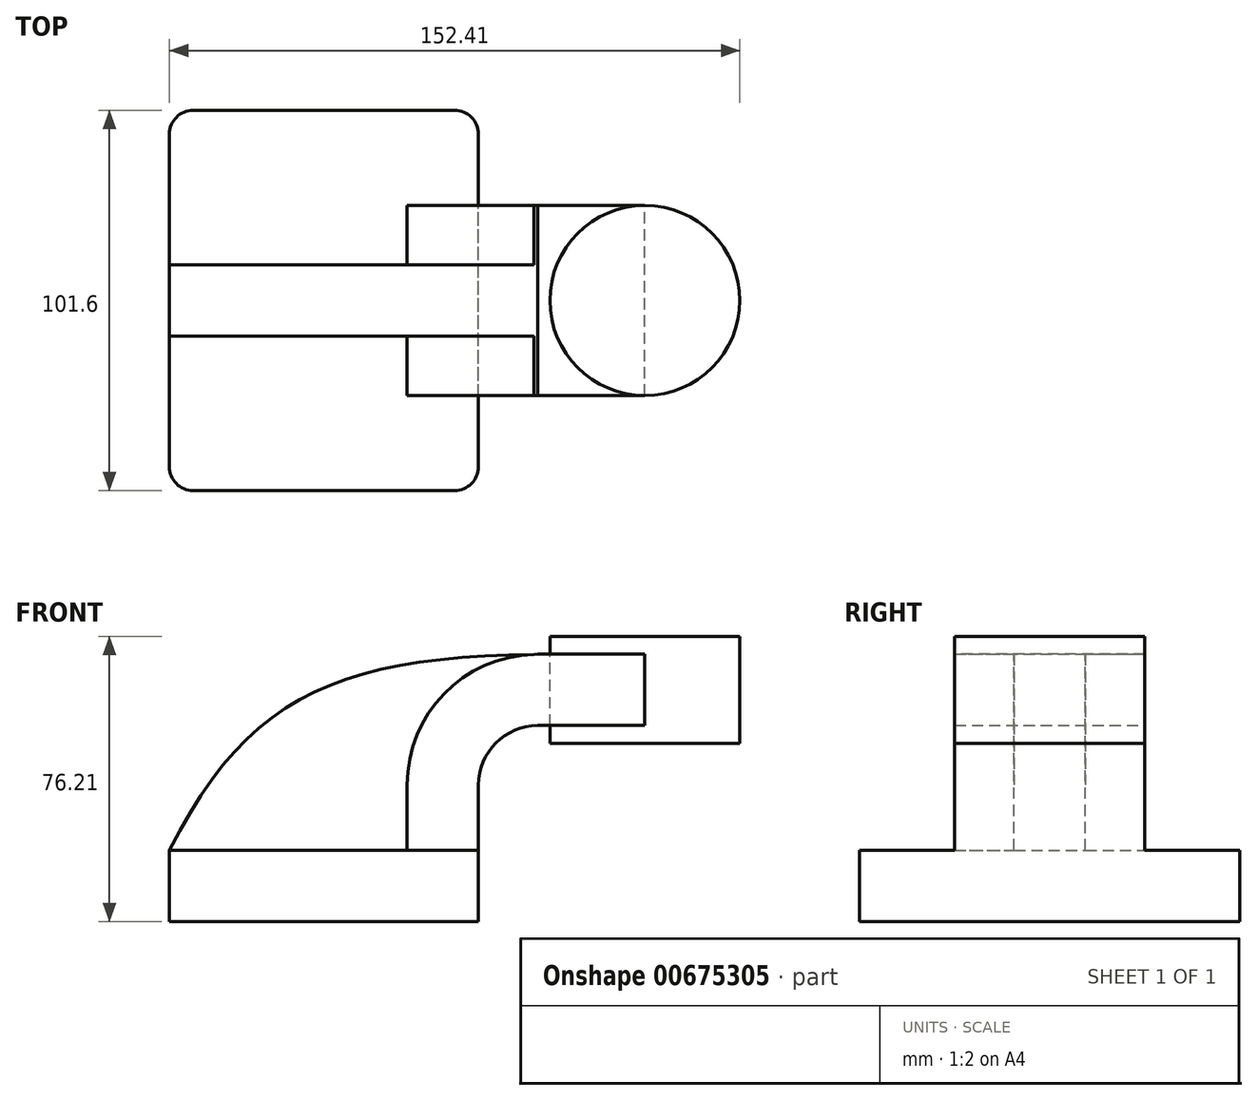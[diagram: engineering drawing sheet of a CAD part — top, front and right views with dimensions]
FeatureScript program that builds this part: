
annotation { "Feature Type Name" : "Feature", "Feature Type Description" : "" }
export const myFeature = defineFeature(function(context is Context, id is Id, definition is map)
    precondition{}
    {
        {
            var Q0;
            Q0=qCreatedBy(makeId("Front.planeOp"),FACE);
            var sketch = newSketch(context, id + "F0", { "sketchPlane" : qUnion([Q0])});
            skLineSegment(sketch, "E0.bottom", {"start": v(41.28, -9.52) * mm, "end": v(-41.28, -9.52) * mm});
            skLineSegment(sketch, "E0.top", {"start": v(41.28, 9.53) * mm, "end": v(-41.28, 9.53) * mm});
            skLineSegment(sketch, "E0.left", {"start": v(41.28, -9.52) * mm, "end": v(41.28, 9.53) * mm});
            skLineSegment(sketch, "E0.right", {"start": v(-41.28, -9.52) * mm, "end": v(-41.28, 9.53) * mm});
            skPoint(sketch, "E0.middle", {"position": v(0, 0) * mm});
            skLineSegment(sketch, "E1.bottom", {"start": v(111.12, 38.1) * mm, "end": v(60.32, 38.1) * mm});
            skLineSegment(sketch, "E1.top", {"start": v(111.12, 66.68) * mm, "end": v(60.32, 66.68) * mm});
            skLineSegment(sketch, "E1.left", {"start": v(111.12, 38.1) * mm, "end": v(111.12, 66.68) * mm});
            skLineSegment(sketch, "E1.right", {"start": v(60.32, 38.1) * mm, "end": v(60.32, 66.68) * mm});
            skPoint(sketch, "E1.middle", {"position": v(85.72, 52.39) * mm});
            skLineSegment(sketch, "E2", {"start": v(41.28, 9.53) * mm, "end": v(41.28, 27) * mm});
            skArc(sketch, "E3", {"start": v(41.27, 27) * mm, "mid": v(45.92, 38.23) * mm, "end": v(57.15, 42.88) * mm});
            skLineSegment(sketch, "E4", {"start": v(57.15, 42.88) * mm, "end": v(85.74, 42.88) * mm});
            skLineSegment(sketch, "E5.0", {"start": v(57.15, 61.93) * mm, "end": v(85.74, 61.93) * mm});
            skArc(sketch, "E5.1", {"start": v(22.23, 27) * mm, "mid": v(32.45, 51.7) * mm, "end": v(57.15, 61.93) * mm});
            skLineSegment(sketch, "E5.2", {"start": v(22.23, 9.53) * mm, "end": v(22.23, 27) * mm});
            skLineSegment(sketch, "E6", {"start": v(85.74, 66.68) * mm, "end": v(85.74, 38.1) * mm});
            skFitSpline(sketch, "E7", {"points": [v(-41.28, 9.53) * mm, v(57.15, 61.93) * mm], "startDerivative": vector(62.63, 124.18) * mm, "endDerivative": vector(160.37, 2.18) * mm});
            skSolve(sketch);
        }
        {
            var Q0;
            Q0=makeQuery(id+"F0.imprint","IMPRINT",FACE,{"disambiguationData":[TD([[makeQuery(id+"F0.imprint","IMPRINT",EDGE,{"derivedFrom":sQuery(id+"F0.wireOp",EDGE,"E0.bottom")}),-1.0]])]});
            extrude(context, id + "F1", {"entities" : qUnion([Q0]), "endBound" : BoundingType.SYMMETRIC, "depth" : 101.6 * mm, "offsetDistance" : 25.4 * mm});
        }
        {
            var Q0;
            {var subQ1=sQuery(id+"F0.wireOp",EDGE,"E2");Q0=makeQuery(id+"F0.imprint","IMPRINT",FACE,{"disambiguationData":[TD([[makeQuery(id+"F0.imprint","IMPRINT",EDGE,{"derivedFrom":subQ1}),1.0]])]});}
            var Q1;
            {var subQ0=sQuery(id+"F0.wireOp",EDGE,"E4");var subQ1=sQuery(id+"F0.wireOp",EDGE,"E1.right");var subQ2=makeQuery(id+"F0.imprint","INTERSECT",VERTEX,{"derivedFrom":[subQ1,subQ0]});Q1=makeQuery(id+"F0.imprint","IMPRINT",FACE,{"disambiguationData":[TD([[makeQuery(id+"F0.imprint","IMPRINT",EDGE,{"disambiguationData":[TD([[subQ2,-1.0]])],"derivedFrom":subQ1}),-1.0]])]});}
            extrude(context, id + "F2", {"entities" : qUnion([Q0, Q1]), "operationType" : NewBodyOperationType.ADD, "endBound" : BoundingType.SYMMETRIC, "depth" : 50.8 * mm, "offsetDistance" : 25.4 * mm});
        }
        {
            var Q0;
            {var subQ3=sQuery(id+"F0.wireOp",EDGE,"E5.2");Q0=makeQuery(id+"F0.imprint","IMPRINT",FACE,{"disambiguationData":[TD([[makeQuery(id+"F0.imprint","IMPRINT",EDGE,{"derivedFrom":subQ3}),1.0]])]});}
            extrude(context, id + "F3", {"entities" : qUnion([Q0]), "operationType" : NewBodyOperationType.ADD, "endBound" : BoundingType.SYMMETRIC, "depth" : 19.05 * mm, "offsetDistance" : 25.4 * mm});
        }
        {
            var Q0;
            {var subQ0=sQuery(id+"F0.wireOp",EDGE,"E1.left");Q0=makeQuery(id+"F0.imprint","IMPRINT",FACE,{"disambiguationData":[TD([[makeQuery(id+"F0.imprint","IMPRINT",EDGE,{"derivedFrom":subQ0}),1.0]])]});}
            var Q1;
            Q1=sQuery(id+"F0.wireOp",EDGE,"E6");
            revolve(context, id + "F4", {"entities" : qUnion([Q0]), "axis" : qUnion([Q1]), "revolveType" : RevolveType.FULL});
        }
        {
            var Q0;
            Q0=makeQuery(id+"F1.opExtrude","CAP_EDGE",EDGE,{"disambiguationData":[OSD([sQuery(id+"F0.wireOp",EDGE,"E0.left")])],"isStart":false});
            var Q1;
            Q1=makeQuery(id+"F1.opExtrude","CAP_EDGE",EDGE,{"disambiguationData":[OSD([sQuery(id+"F0.wireOp",EDGE,"E0.right")])],"isStart":false});
            var Q2;
            Q2=makeQuery(id+"F1.opExtrude","CAP_EDGE",EDGE,{"disambiguationData":[OSD([sQuery(id+"F0.wireOp",EDGE,"E0.right")])],"isStart":true});
            var Q3;
            Q3=makeQuery(id+"F1.opExtrude","CAP_EDGE",EDGE,{"disambiguationData":[OSD([sQuery(id+"F0.wireOp",EDGE,"E0.left")])],"isStart":true});
            fillet(context, id + "F5", {"entities" : qUnion([Q0, Q1, Q2, Q3]), "radius" : 6.35 * mm, "tangentPropagation" : true, "allowEdgeOverflow" : false});
        }
    });
